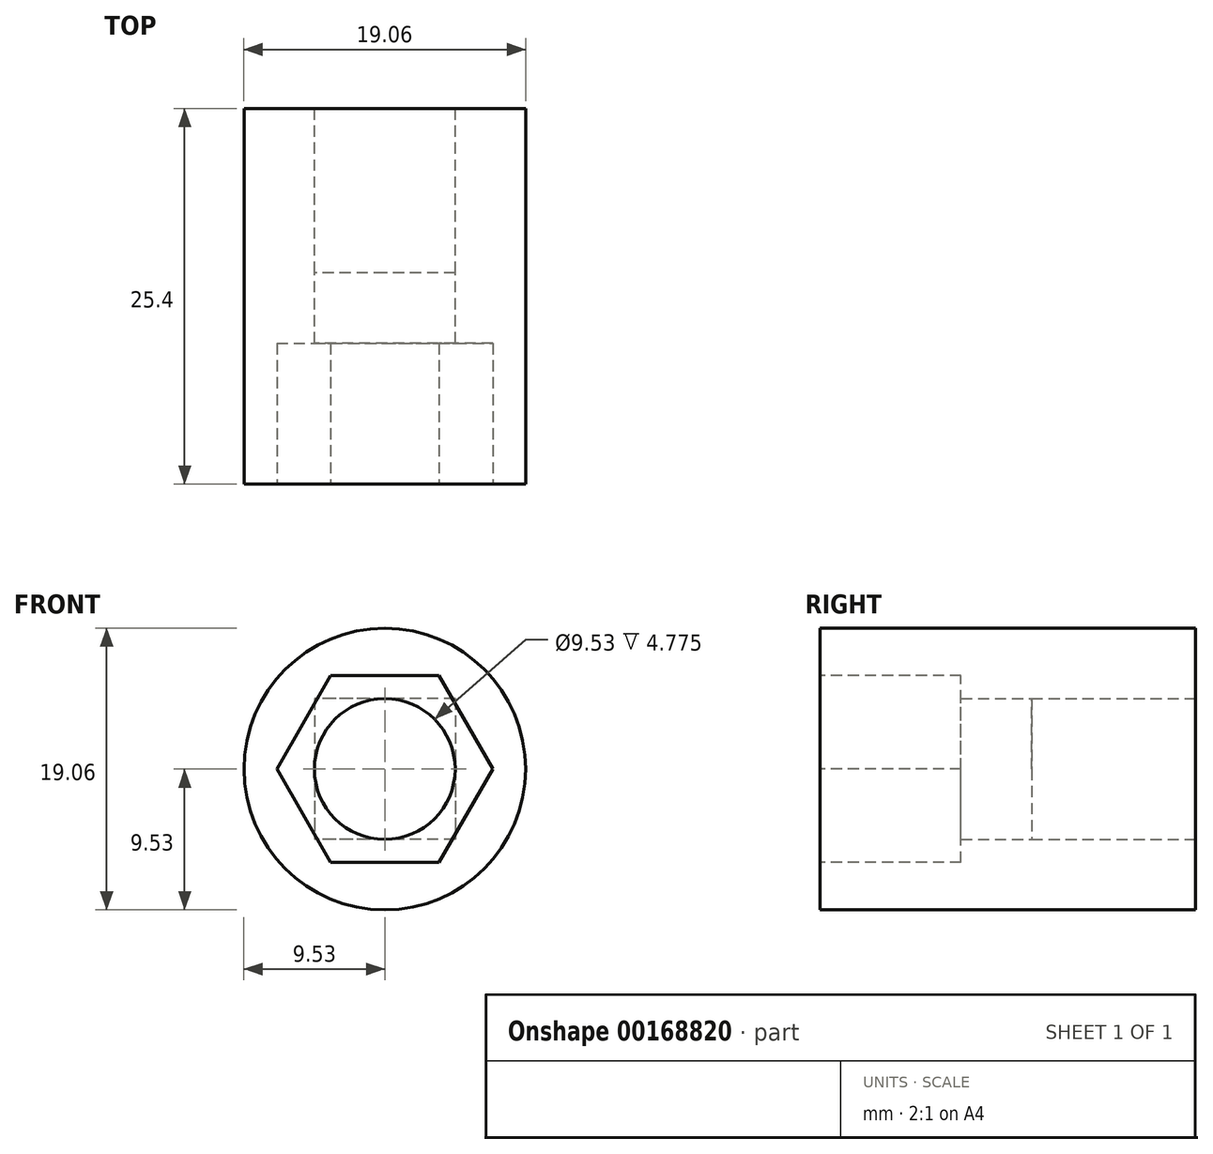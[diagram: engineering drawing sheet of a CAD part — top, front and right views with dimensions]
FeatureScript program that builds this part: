
annotation { "Feature Type Name" : "Feature", "Feature Type Description" : "" }
export const myFeature = defineFeature(function(context is Context, id is Id, definition is map)
    precondition{}
    {
        {
            var Q0;
            Q0=qCreatedBy(makeId("Front.planeOp"),FACE);
            var sketch = newSketch(context, id + "F0", { "sketchPlane" : qUnion([Q0])});
            skCircle(sketch, "E0", {"center": v(0, 0) * mm, "radius": 9.53 * mm});
            skSolve(sketch);
        }
        {
            var Q0;
            Q0 = qSketchRegion(id + "F0", true);
            extrude(context, id + "F1", {"entities" : qUnion([Q0]), "depth" : 25.4 * mm});
        }
        {
            var Q0;
            Q0=qCreatedBy(makeId("Front.planeOp"),FACE);
            var sketch = newSketch(context, id + "F2", { "sketchPlane" : qUnion([Q0])});
            skLineSegment(sketch, "E1.bottom", {"start": v(4.76, 4.76) * mm, "end": v(-4.76, 4.76) * mm});
            skLineSegment(sketch, "E1.top", {"start": v(4.76, -4.76) * mm, "end": v(-4.76, -4.76) * mm});
            skLineSegment(sketch, "E1.left", {"start": v(4.76, 4.76) * mm, "end": v(4.76, -4.76) * mm});
            skLineSegment(sketch, "E1.right", {"start": v(-4.76, 4.76) * mm, "end": v(-4.76, -4.76) * mm});
            skPoint(sketch, "E1.middle", {"position": v(0, 0) * mm});
            skCircle(sketch, "E2", {"center": v(0, 0) * mm, "radius": 4.76 * mm});
            skSolve(sketch);
        }
        {
            var Q0;
            {var subQ0=sQuery(id+"F2.wireOp",EDGE,"E2");var subQ1=makeQuery(id+"F2.imprint","INTERSECT",VERTEX,{"derivedFrom":[sQuery(id+"F2.wireOp",EDGE,"E1.bottom"),subQ0]});Q0=makeQuery(id+"F2.imprint","IMPRINT",FACE,{"disambiguationData":[TD([[makeQuery(id+"F2.imprint","IMPRINT",EDGE,{"disambiguationData":[TD([[subQ1,1.0]])],"derivedFrom":subQ0}),1.0]])]});}
            extrude(context, id + "F3", {"entities" : qUnion([Q0]), "operationType" : NewBodyOperationType.REMOVE, "endBound" : BoundingType.THROUGH_ALL, "depth" : 25.4 * mm});
        }
        {
            var Q0;
            Q0 = qSketchRegion(id + "F2", true);
            var Q1;
            Q1=makeQuery(id+"F1.opExtrude","CAP_FACE",FACE,{"disambiguationData":[OSD([sQuery(id+"F0.wireOp",EDGE,"E0")])],"isStart":false});
            extrude(context, id + "F4", {"entities" : qUnion([Q0, Q1]), "operationType" : NewBodyOperationType.REMOVE, "depth" : 11.1 * mm});
        }
        {
            var Q0;
            Q0=makeQuery(id+"F1.opExtrude","CAP_FACE",FACE,{"disambiguationData":[OSD([sQuery(id+"F0.wireOp",EDGE,"E0")])],"isStart":false});
            var sketch = newSketch(context, id + "F5", { "sketchPlane" : qUnion([Q0])});
            skCircle(sketch, "E3.cCircle", {"center": v(0, 0) * mm, "radius": 6.32 * mm, "construction": true});
            skLineSegment(sketch, "E3.0", {"start": v(-3.65, 6.32) * mm, "end": v(3.65, 6.32) * mm});
            skLineSegment(sketch, "E3.1", {"start": v(3.65, 6.32) * mm, "end": v(7.3, 0) * mm});
            skLineSegment(sketch, "E3.2", {"start": v(7.3, 0) * mm, "end": v(3.65, -6.32) * mm});
            skLineSegment(sketch, "E3.3", {"start": v(3.65, -6.32) * mm, "end": v(-3.65, -6.32) * mm});
            skLineSegment(sketch, "E3.4", {"start": v(-3.65, -6.32) * mm, "end": v(-7.3, 0) * mm});
            skLineSegment(sketch, "E3.5", {"start": v(-7.3, 0) * mm, "end": v(-3.65, 6.32) * mm});
            skPoint(sketch, "E3.0.midPoint", {"position": v(0, 6.32) * mm});
            skSolve(sketch);
        }
        {
            var Q0;
            Q0=makeQuery(id+"F5.imprint","IMPRINT",FACE,{"disambiguationData":[TD([[makeQuery(id+"F5.imprint","IMPRINT",EDGE,{"derivedFrom":sQuery(id+"F5.wireOp",EDGE,"E3.0")}),-1.0]])]});
            extrude(context, id + "F6", {"entities" : qUnion([Q0]), "operationType" : NewBodyOperationType.REMOVE, "oppositeDirection" : true, "depth" : 9.52 * mm});
        }
    });
